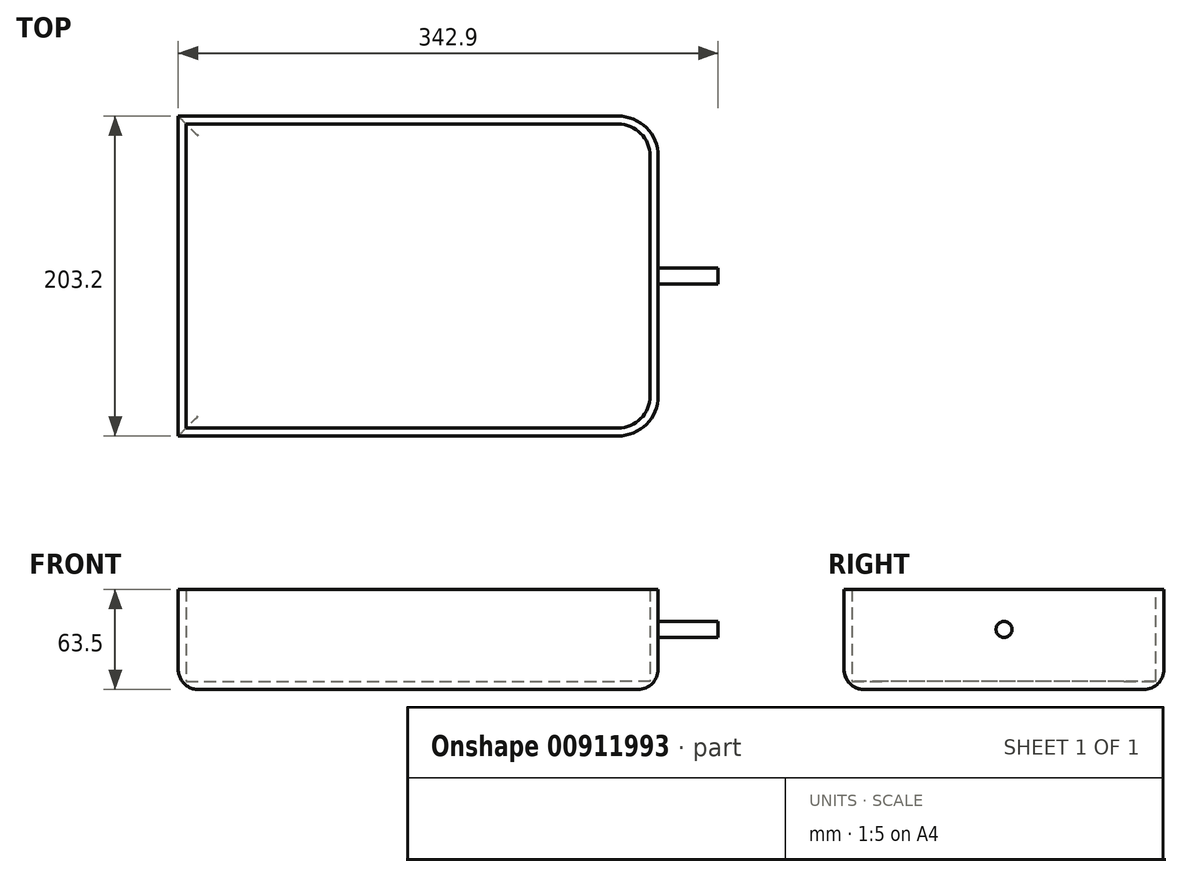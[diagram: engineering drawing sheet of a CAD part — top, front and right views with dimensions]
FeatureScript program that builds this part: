
annotation { "Feature Type Name" : "Feature", "Feature Type Description" : "" }
export const myFeature = defineFeature(function(context is Context, id is Id, definition is map)
    precondition{}
    {
        {
            var Q0;
            Q0=qCreatedBy(makeId("Top.planeOp"),FACE);
            var sketch = newSketch(context, id + "F0", { "sketchPlane" : qUnion([Q0])});
            skLineSegment(sketch, "E0.bottom", {"start": v(-401.16, 176.29) * mm, "end": v(-121.76, 176.29) * mm});
            skLineSegment(sketch, "E0.top", {"start": v(-401.16, -26.91) * mm, "end": v(-121.76, -26.91) * mm});
            skLineSegment(sketch, "E0.left", {"start": v(-401.16, 176.29) * mm, "end": v(-401.16, -26.91) * mm});
            skLineSegment(sketch, "E0.right", {"start": v(-96.36, 150.89) * mm, "end": v(-96.36, -1.51) * mm});
            skLineSegment(sketch, "E1.left", {"start": v(-96.36, 44.6) * mm, "end": v(-96.36, 6.5) * mm});
            skPoint(sketch, "E2.visualSharp", {"position": v(-96.36, 176.29) * mm});
            skArc(sketch, "E2.filletArc", {"start": v(-96.36, 150.89) * mm, "mid": v(-103.8, 168.85) * mm, "end": v(-121.76, 176.29) * mm});
            skPoint(sketch, "E3.visualSharp", {"position": v(-96.36, -26.91) * mm});
            skArc(sketch, "E3.filletArc", {"start": v(-121.76, -26.91) * mm, "mid": v(-103.8, -19.47) * mm, "end": v(-96.36, -1.51) * mm});
            skLineSegment(sketch, "E4.bottom", {"start": v(-401.16, 176.29) * mm, "end": v(-344.3, 176.29) * mm});
            skLineSegment(sketch, "E4.top", {"start": v(-401.16, -26.91) * mm, "end": v(-344.3, -26.91) * mm});
            skSolve(sketch);
        }
        {
            var Q0;
            Q0=makeQuery(id+"F0.imprint","IMPRINT",FACE,{"disambiguationData":[TD([[makeQuery(id+"F0.imprint","IMPRINT",EDGE,{"derivedFrom":sQuery(id+"F0.wireOp",EDGE,"E0.bottom")}),-1.0]])]});
            extrude(context, id + "F1", {"entities" : qUnion([Q0]), "depth" : 63.5 * mm, "offsetDistance" : 25.4 * mm});
        }
        {
            var Q0;
            Q0=makeQuery(id+"F1.opExtrude","CAP_FACE",FACE,{"disambiguationData":[OSD([sQuery(id+"F0.wireOp",EDGE,"E0.bottom"),sQuery(id+"F0.wireOp",EDGE,"E0.top"),sQuery(id+"F0.wireOp",EDGE,"E0.left"),sQuery(id+"F0.wireOp",EDGE,"E0.right"),sQuery(id+"F0.wireOp",EDGE,"E1.left")])],"isStart":false});
            var Q1;
            Q1=makeQuery(id+"F1.opExtrude","SWEPT_FACE",FACE,{"disambiguationData":[OSD([sQuery(id+"F0.wireOp",EDGE,"E0.left")])]});
            shell(context, id + "F2", {"entities" : qUnion([Q0, Q1]), "thickness" : 5.08 * mm});
        }
        {
            var Q0;
            Q0=makeQuery(id+"F1.opExtrude","SWEPT_FACE",FACE,{"disambiguationData":[OSD([sQuery(id+"F0.wireOp",EDGE,"E0.right"),sQuery(id+"F0.wireOp",EDGE,"E1.left")])]});
            var sketch = newSketch(context, id + "F3", { "sketchPlane" : qUnion([Q0])});
            skCircle(sketch, "E5", {"center": v(74.69, 38.1) * mm, "radius": 5.08 * mm});
            skSolve(sketch);
        }
        {
            var Q0;
            Q0=makeQuery(id+"F3.imprint","IMPRINT",FACE,{"disambiguationData":[TD([[makeQuery(id+"F3.imprint","IMPRINT",EDGE,{"derivedFrom":sQuery(id+"F3.wireOp",EDGE,"E5")}),1.0]])]});
            var Q1;
            Q1=sQuery(id+"F3.wireOp",EDGE,"E5");
            extrude(context, id + "F4", {"entities" : qUnion([Q0]), "operationType" : NewBodyOperationType.ADD, "surfaceEntities" : qUnion([Q1]), "depth" : 38.1 * mm, "offsetDistance" : 25.4 * mm});
        }
        {
            var Q0;
            Q0=makeQuery(id+"F1.opExtrude","CAP_FACE",FACE,{"disambiguationData":[OSD([sQuery(id+"F0.wireOp",EDGE,"E0.bottom"),sQuery(id+"F0.wireOp",EDGE,"E0.top"),sQuery(id+"F0.wireOp",EDGE,"E0.right"),sQuery(id+"F0.wireOp",EDGE,"E1.left"),sQuery(id+"F0.wireOp",EDGE,"E2.filletArc"),sQuery(id+"F0.wireOp",EDGE,"E3.filletArc"),sQuery(id+"F0.wireOp",EDGE,"E4.bottom"),sQuery(id+"F0.wireOp",EDGE,"E4.top"),sQuery(id+"F0.wireOp",EDGE,"E0.left")])],"isStart":true});
            fillet(context, id + "F5", {"entities" : qUnion([Q0]), "radius" : 12.7 * mm, "tangentPropagation" : true, "allowEdgeOverflow" : false});
        }
    });
